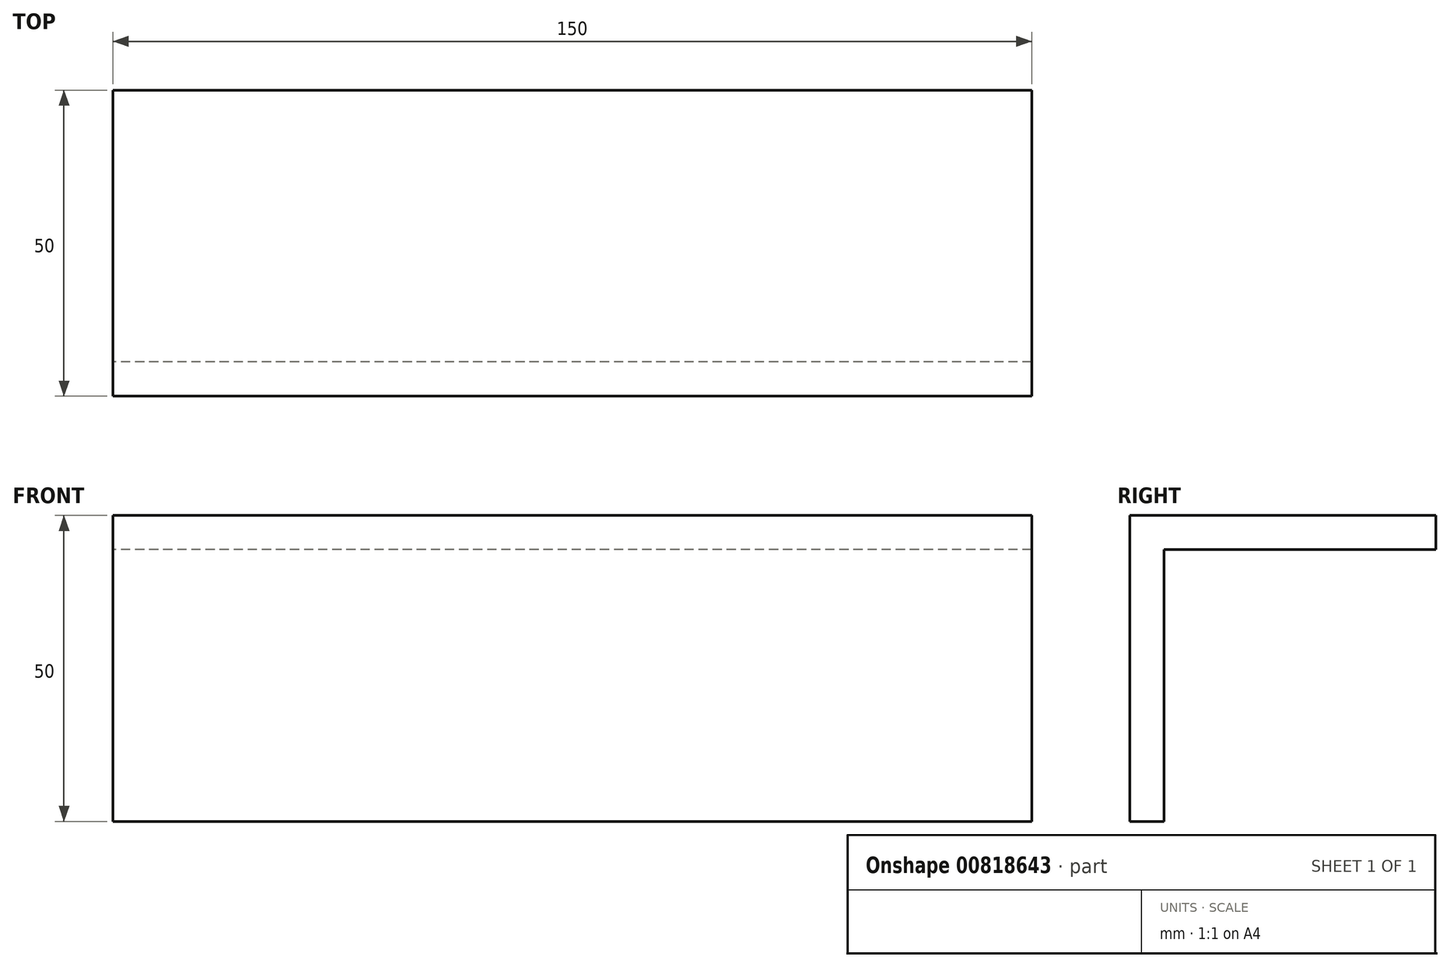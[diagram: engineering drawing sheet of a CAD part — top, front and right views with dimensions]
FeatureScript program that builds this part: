
annotation { "Feature Type Name" : "Feature", "Feature Type Description" : "" }
export const myFeature = defineFeature(function(context is Context, id is Id, definition is map)
    precondition{}
    {
        {
            var Q0;
            Q0=qCreatedBy(makeId("Right.planeOp"),FACE);
            var sketch = newSketch(context, id + "F0", { "sketchPlane" : qUnion([Q0])});
            skLineSegment(sketch, "E0", {"start": v(0, 0) * mm, "end": v(50, 0) * mm});
            skLineSegment(sketch, "E1", {"start": v(50, 0) * mm, "end": v(50, -5.6) * mm});
            skLineSegment(sketch, "E2", {"start": v(50, -5.6) * mm, "end": v(5.6, -5.6) * mm});
            skLineSegment(sketch, "E3", {"start": v(5.6, -5.6) * mm, "end": v(5.6, -50) * mm});
            skLineSegment(sketch, "E4", {"start": v(5.6, -50) * mm, "end": v(0, -50) * mm});
            skLineSegment(sketch, "E5", {"start": v(0, -50) * mm, "end": v(0, 0) * mm});
            skSolve(sketch);
        }
        {
            var Q0;
            Q0=makeQuery(id+"F0.imprint","IMPRINT",FACE,{"disambiguationData":[TD([[makeQuery(id+"F0.imprint","IMPRINT",EDGE,{"derivedFrom":sQuery(id+"F0.wireOp",EDGE,"E0")}),-1.0]])]});
            extrude(context, id + "F1", {"entities" : qUnion([Q0]), "endBound" : BoundingType.SYMMETRIC, "depth" : 150 * mm, "offsetDistance" : 25 * mm});
        }
    });
